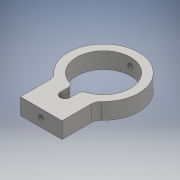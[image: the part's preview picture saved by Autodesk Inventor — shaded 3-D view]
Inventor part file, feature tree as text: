
AUTODESK INVENTOR PART (.ipt)
format: ipt  version: 2016 (Build 200138000, 138)  size: 162,304 bytes
history: native  units: mm
features: sketch x3, extrude x2, fillet x2, hole x2, plane x2
ambient origin geometry x8: Origin, YZ Plane, XZ Plane, XY Plane, X Axis, Y Axis, Z Axis, Center Point
bodies: Solid1 (feature_tree)
feature tree (11):
  extrude  "Extrusion1"  Depth=33.0mm
  fillet  "Fillet2"  Radius=43.0mm
  hole  "Hole1"  [1 undecoded]
  plane  "Work Plane1"
  hole  "Hole2"  [1 undecoded]
  extrude  "Extrusion3"  Depth=6.0mm
  fillet  "Fillet4"  [1 undecoded]
  plane  "Work Plane2"
  sketch  "Sketch1"  dims[d0=30.0mm d1=33.0mm d2=43.0mm]
  sketch  "Sketch3"  dims[d4=10.0mm d5=0.0mm d7=25.4mm]
  sketch  "Sketch4"  dims[d8=38.1mm d9=6.0mm d14=3.242mm d15=8.0mm d16=4.0mm d17=2.0mm d18=90.0deg d19=10.0mm d20=20.594885mm d21=3.302mm d22=8.331mm d23=4.0mm d24=2.0mm d25=90.0deg d26=12.3mm d27=20.594885mm d28=6.0mm d29=0.0mm d30=0.0mm d31=3.0mm d32=10.0mm]
note: 3 required parameter values undecoded (feature->parameter linkage not recoverable at this tier; creation-order binding heuristic only, values carry confidence <= 0.55)
